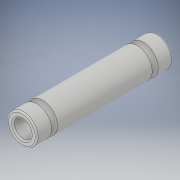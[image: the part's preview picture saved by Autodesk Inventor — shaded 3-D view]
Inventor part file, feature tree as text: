
AUTODESK INVENTOR PART (.ipt)
format: ipt  version: 2018 (Build 220112000, 112)  size: 158,720 bytes
history: native  units: mm
features: revolve x1, fillet x1, sketch x1
ambient origin geometry x8: Origin, YZ Plane, XZ Plane, XY Plane, X Axis, Y Axis, Z Axis, Center Point
bodies: Solid1 (feature_tree)
feature tree (3):
  revolve  "Revolution1"  [1 undecoded]
  fillet  "Fillet1"  Radius=1.0mm
  sketch  "Sketch1"  dims[d1=2.5mm d2=1.5mm d3=3.0mm d4=1.0mm d5=0.25mm d6=2.25mm d7=1.0mm d8=23.0mm d9=90.0deg d10=0.25mm]
note: 1 required parameter value undecoded (feature->parameter linkage not recoverable at this tier; creation-order binding heuristic only, values carry confidence <= 0.55)
